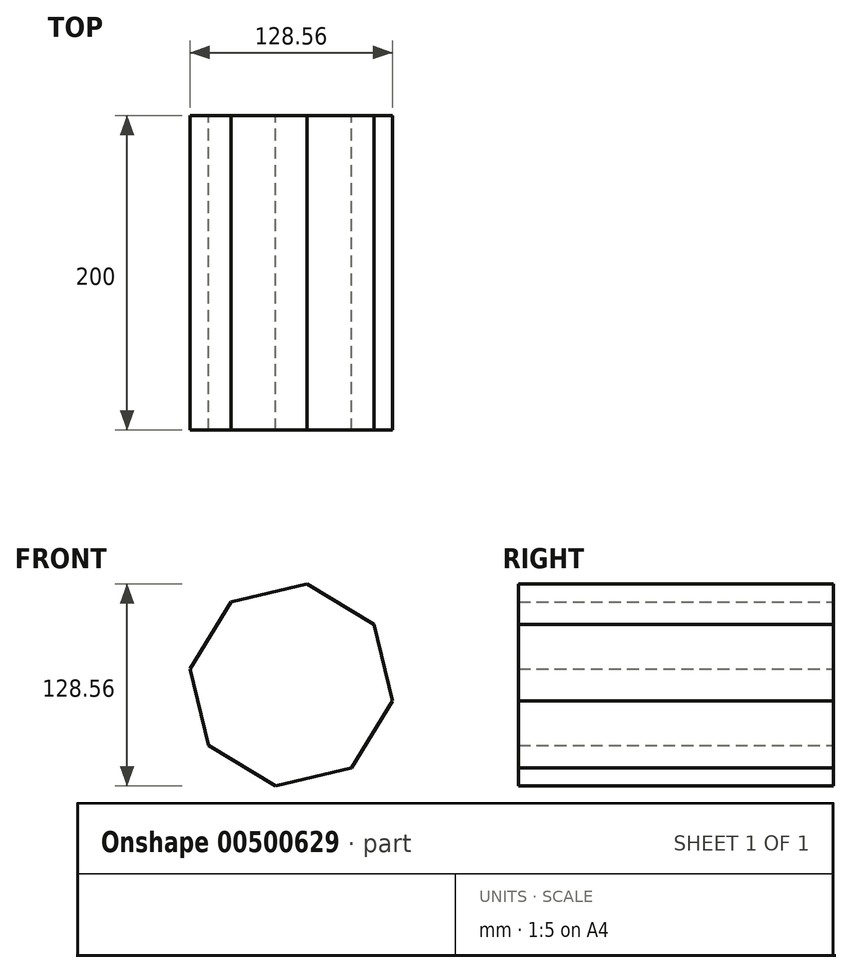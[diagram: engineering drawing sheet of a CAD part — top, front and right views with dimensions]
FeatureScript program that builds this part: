
annotation { "Feature Type Name" : "Feature", "Feature Type Description" : "" }
export const myFeature = defineFeature(function(context is Context, id is Id, definition is map)
    precondition{}
    {
        {
            var Q0;
            Q0=qCreatedBy(makeId("Front.planeOp"),FACE);
            var sketch = newSketch(context, id + "F0", { "sketchPlane" : qUnion([Q0])});
            skCircle(sketch, "E0.cCircle", {"center": v(0, 0) * mm, "radius": 60.11 * mm, "construction": true});
            skLineSegment(sketch, "E0.0", {"start": v(64.28, -10.08) * mm, "end": v(38.32, -52.58) * mm});
            skLineSegment(sketch, "E0.1", {"start": v(38.32, -52.58) * mm, "end": v(-10.08, -64.28) * mm});
            skLineSegment(sketch, "E0.2", {"start": v(-10.08, -64.28) * mm, "end": v(-52.58, -38.32) * mm});
            skLineSegment(sketch, "E0.3", {"start": v(-52.58, -38.32) * mm, "end": v(-64.28, 10.08) * mm});
            skLineSegment(sketch, "E0.4", {"start": v(-64.28, 10.08) * mm, "end": v(-38.32, 52.58) * mm});
            skLineSegment(sketch, "E0.5", {"start": v(-38.32, 52.58) * mm, "end": v(10.08, 64.28) * mm});
            skLineSegment(sketch, "E0.6", {"start": v(10.08, 64.28) * mm, "end": v(52.58, 38.32) * mm});
            skLineSegment(sketch, "E0.7", {"start": v(52.58, 38.32) * mm, "end": v(64.28, -10.08) * mm});
            skPoint(sketch, "E0.0.midPoint", {"position": v(51.3, -31.33) * mm});
            skSolve(sketch);
        }
        {
            var Q0;
            Q0=makeQuery(id+"F0.imprint","IMPRINT",FACE,{"disambiguationData":[TD([[makeQuery(id+"F0.imprint","IMPRINT",EDGE,{"derivedFrom":sQuery(id+"F0.wireOp",EDGE,"E0.0")}),-1.0]])]});
            extrude(context, id + "F1", {"entities" : qUnion([Q0]), "depth" : 200 * mm});
        }
    });
